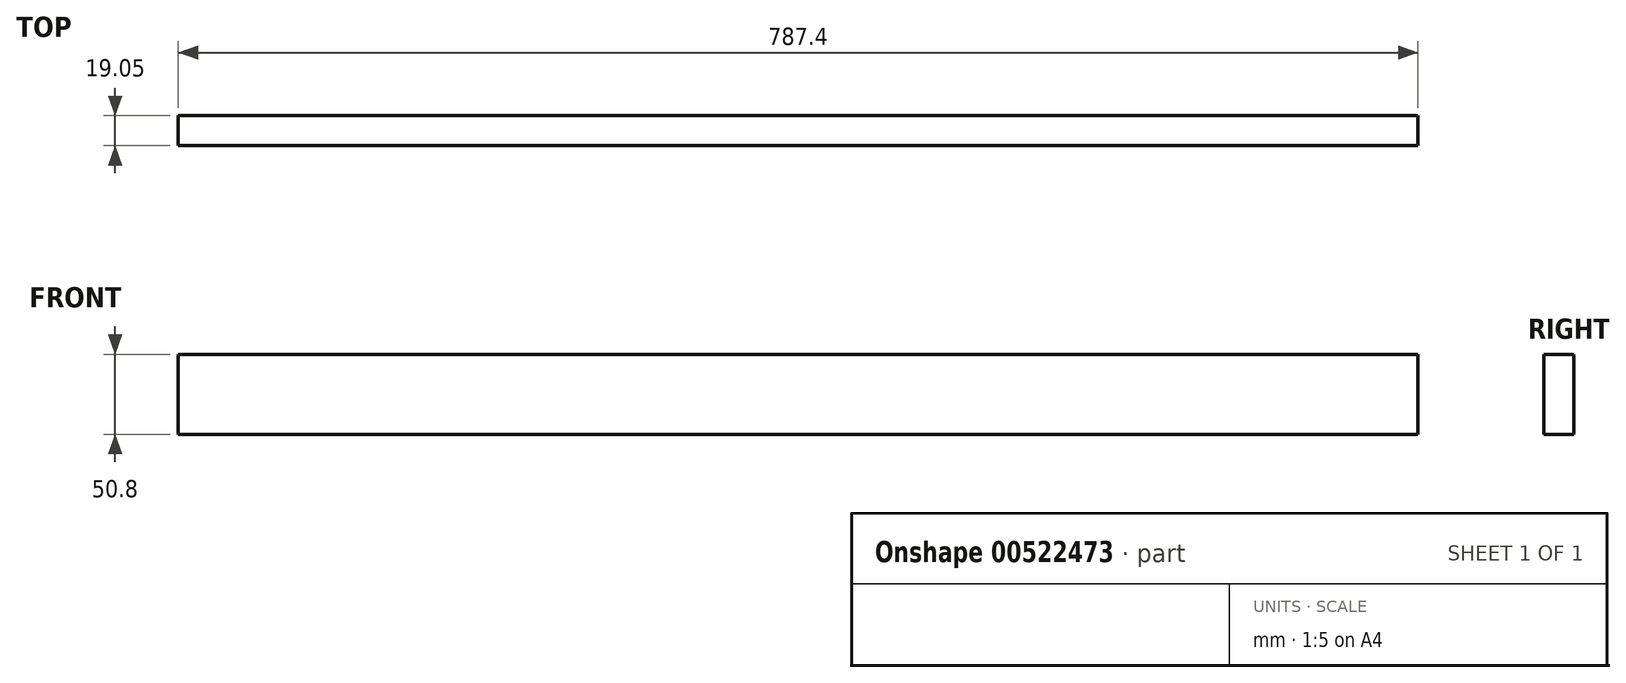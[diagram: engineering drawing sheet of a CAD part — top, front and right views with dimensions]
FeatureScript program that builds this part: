
annotation { "Feature Type Name" : "Feature", "Feature Type Description" : "" }
export const myFeature = defineFeature(function(context is Context, id is Id, definition is map)
    precondition{}
    {
        {
            var Q0;
            Q0=qCreatedBy(makeId("Top.planeOp"),FACE);
            var sketch = newSketch(context, id + "F0", { "sketchPlane" : qUnion([Q0])});
            skLineSegment(sketch, "E0.bottom", {"start": v(-253.72, -29.25) * mm, "end": v(533.68, -29.25) * mm});
            skLineSegment(sketch, "E0.top", {"start": v(-253.72, -48.3) * mm, "end": v(533.68, -48.3) * mm});
            skLineSegment(sketch, "E0.left", {"start": v(-253.72, -29.25) * mm, "end": v(-253.72, -48.3) * mm});
            skLineSegment(sketch, "E0.right", {"start": v(533.68, -29.25) * mm, "end": v(533.68, -48.3) * mm});
            skSolve(sketch);
        }
        {
            var Q0;
            Q0=makeQuery(id+"F0.imprint","IMPRINT",FACE,{"disambiguationData":[TD([[makeQuery(id+"F0.imprint","IMPRINT",EDGE,{"derivedFrom":sQuery(id+"F0.wireOp",EDGE,"E0.bottom")}),-1.0]])]});
            extrude(context, id + "F1", {"entities" : qUnion([Q0]), "depth" : 50.8 * mm, "offsetDistance" : 25.4 * mm});
        }
    });
